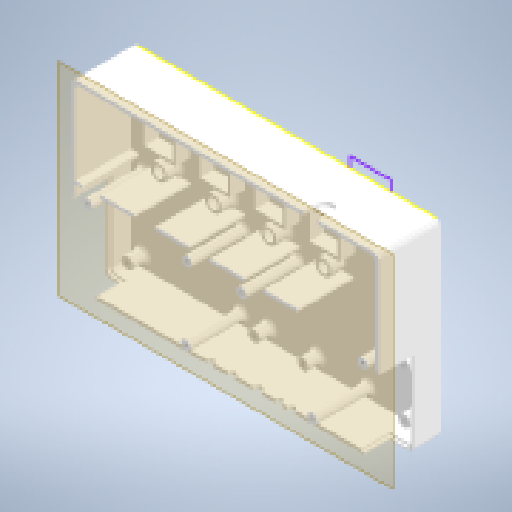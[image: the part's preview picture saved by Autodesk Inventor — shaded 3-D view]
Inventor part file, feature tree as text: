
AUTODESK INVENTOR PART (.ipt)
format: ipt  version: 2024.2 (Build 282272000, 272)  size: 901,632 bytes
history: native  units: in
note: dims shown in document units (in); Inventor stores cm internally (conversion verified against a paired STEP export)
features: reference x55, extrude x17, other x13, projected_geometry x13, fillet x4, hole x3, sketch x3, plane x2, chamfer x1
ambient origin geometry x8: Origin, YZ Plane, XZ Plane, XY Plane, X Axis, Y Axis, Z Axis, Center Point
bodies: Solid1 (feature_tree)
feature tree (111):
  extrude  "BasePlate"  Depth=8.5in
  plane  "Work Plane1"
  extrude  "PCB Screw Bosses"  Depth=0.315in
  extrude  "OuterCaseWall"  Depth=0.095in
  extrude  "ReceptBottomRibs"  Depth=0.125in TaperAngle=0.0deg
  other  "Top Of Case"
  other  "Offset Top Of Case"
  extrude  "Barriers"  Depth=0.125in TaperAngle=0.0deg
  extrude  "HVSideBosses"  Depth=0.125in TaperAngle=0.0deg
  hole  "HotSideHoles"  [1 undecoded]
  chamfer  "HotSideHoleChamfer"  Distance=1.0in
  extrude  "LogicSideBosses"  Depth=0.125in
  hole  "LogicSideHoles"  [1 undecoded]
  fillet  "Fillet1"  Radius=0.125in
  hole  "PCBMountHoles"  [1 undecoded]
  extrude  "HV Upper Wall"  Depth=0.3937in
  fillet  "HV Corner Fillets"  Radius=0.6in
  extrude  "BossCutPowerSupply"  Depth=0.1969in
  fillet  "LgicCornerFillets"  Radius=1.0in
  extrude  "Extrusion11"  Depth=0.125in
  extrude  "Extrusion12"  Depth=0.125in TaperAngle=0.0deg
  extrude  "OuterWallLip"  Depth=0.125in
  extrude  "Extrusion14"  Depth=0.125in TaperAngle=0.0deg
  extrude  "Extrusion15"  Depth=0.2in
  extrude  "Extrusion16"  Depth=0.125in
  sketch  "Sketch20"  dims[d5=0.0787in d6=0.0in d7=0.095in d8=0.6in d9=0.0in d24=1.0in d25=0.0in d37=1.0in d38=0.0in d40=1.0in d41=0.0in d42=0.129in d43=0.224in d44=0.3in d45=0.1181in d46=0.5635in d47=1.0in d48=0.8108in d50=1.0in d51=0.0in d52=0.0787in d54=0.0849in d55=0.224in d56=0.225in d57=0.25in d58=0.5635in d59=0.7in d60=0.8108in d61=0.125in d62=0.0849in d63=0.125in d64=0.225in d65=0.25in d66=0.5635in d67=1.0in d68=0.8108in d69=0.08in d70=0.125in d71=45.0deg d72=1.0in d73=0.0in d74=0.3937in d76=0.6in d77=0.1969in d78=1.0in d79=0.0in d81=-0.0079in d82=0.125in d83=1.0in d84=0.0in d85=0.125in d88=0.7in d89=0.0in d90=0.2in d91=0.25in d92=0.2in d93=0.75in d94=0.0in d95=0.2in d96=0.2in d97=0.0512in d98=0.0787in d99=0.0in d100=0.0512in d101=0.0787in d102=0.0in d103=0.0787in d104=0.0in d105=0.0787in d106=0.0in d120=2.8677in d134=0.0157in d135=0.0157in d136=0.0157in d137=0.0157in d138=0.0787in d139=0.0394in d140=0.0394in d141=0.0787in d142=0.0787in d143=0.0394in d144=1.5748in d146=1.52in d147=0.3937in d149=1.0in d151=0.2in d153=1.394in d154=1.0in d155=0.0in d158=1.7in d159=1.2in d160=0.125in]
  plane  "Work Plane4"
  extrude  "Extrusion17"  Depth=0.2in
  extrude  "Cord cut"  Depth=0.125in TaperAngle=0.0deg
  fillet  "Fillet4"  Radius=0.2in
  reference  "Reference1"
  reference  "Reference3"
  reference  "Reference4"
  reference  "Reference6"
  reference  "Reference7"
  reference  "Reference8"
  reference  "Reference9"
  reference  "Reference10"
  reference  "Reference11"
  reference  "Reference54"
  reference  "Reference55"
  reference  "Reference56"
  reference  "Reference57"
  reference  "Reference62"
  reference  "Reference67"
  reference  "Reference69"
  reference  "Reference70"
  reference  "Reference71"
  reference  "Reference72"
  sketch  "Sketch9"  dims[d0=8.5in d1=5.2in]
  projected_geometry  "Projected Loop1"
  projected_geometry  "Projected Loop2"
  projected_geometry  "Projected Loop3"
  projected_geometry  "Projected Loop4"
  projected_geometry  "Projected Loop5"
  projected_geometry  "Projected Loop6"
  projected_geometry  "Projected Loop7"
  projected_geometry  "Projected Loop8"
  projected_geometry  "Projected Loop9"
  projected_geometry  "Projected Loop10"
  projected_geometry  "Projected Loop11"
  projected_geometry  "Projected Loop12"
  reference  "Reference73"
  projected_geometry  "Projected Loop13"
  reference  "Reference74"
  reference  "Reference75"
  reference  "Reference76"
  reference  "Reference77"
  reference  "Reference78"
  sketch  "Sketch17"  dims[d2=0.1575in d3=0.0in d4=0.315in]
  reference  "Reference80"
  reference  "Reference81"
  reference  "Reference82"
  reference  "Reference83"
  reference  "Reference84"
  reference  "Reference85"
  reference  "Reference86"
  reference  "Reference87"
  reference  "Reference88"
  reference  "Reference89"
  reference  "Reference91"
  reference  "Reference92"
  reference  "Reference93"
  reference  "Reference94"
  reference  "Reference95"
  reference  "Reference96"
  reference  "Reference97"
  reference  "Reference98"
  reference  "Reference99"
  reference  "Reference100"
  reference  "Reference101"
  reference  "Reference102"
  reference  "Reference103"
  reference  "Reference104"
  reference  "Reference105"
  reference  "Reference106"
  reference  "Reference107"
  reference  "Reference108"
  reference  "Reference109"
  reference  "Reference110"
  other  "<userpath>\Dropbox\elec\Mechanical\ReefVoltEssential\_TOP.iam"
  other  "_TOP.iam"
  other  "reefvolt_power_essentials_ESP32:2"
  other  "reefvolt_power_essentials_ESP32_BOARD:1"
  other  "J403"
  other  "J401"
  other  "J402"
  other  "J200_PLA"
  other  "J200_PLD"
  other  "J200_PLC"
  other  "J200_PLB"
note: 3 required parameter values undecoded (feature->parameter linkage not recoverable at this tier; creation-order binding heuristic only, values carry confidence <= 0.55)
